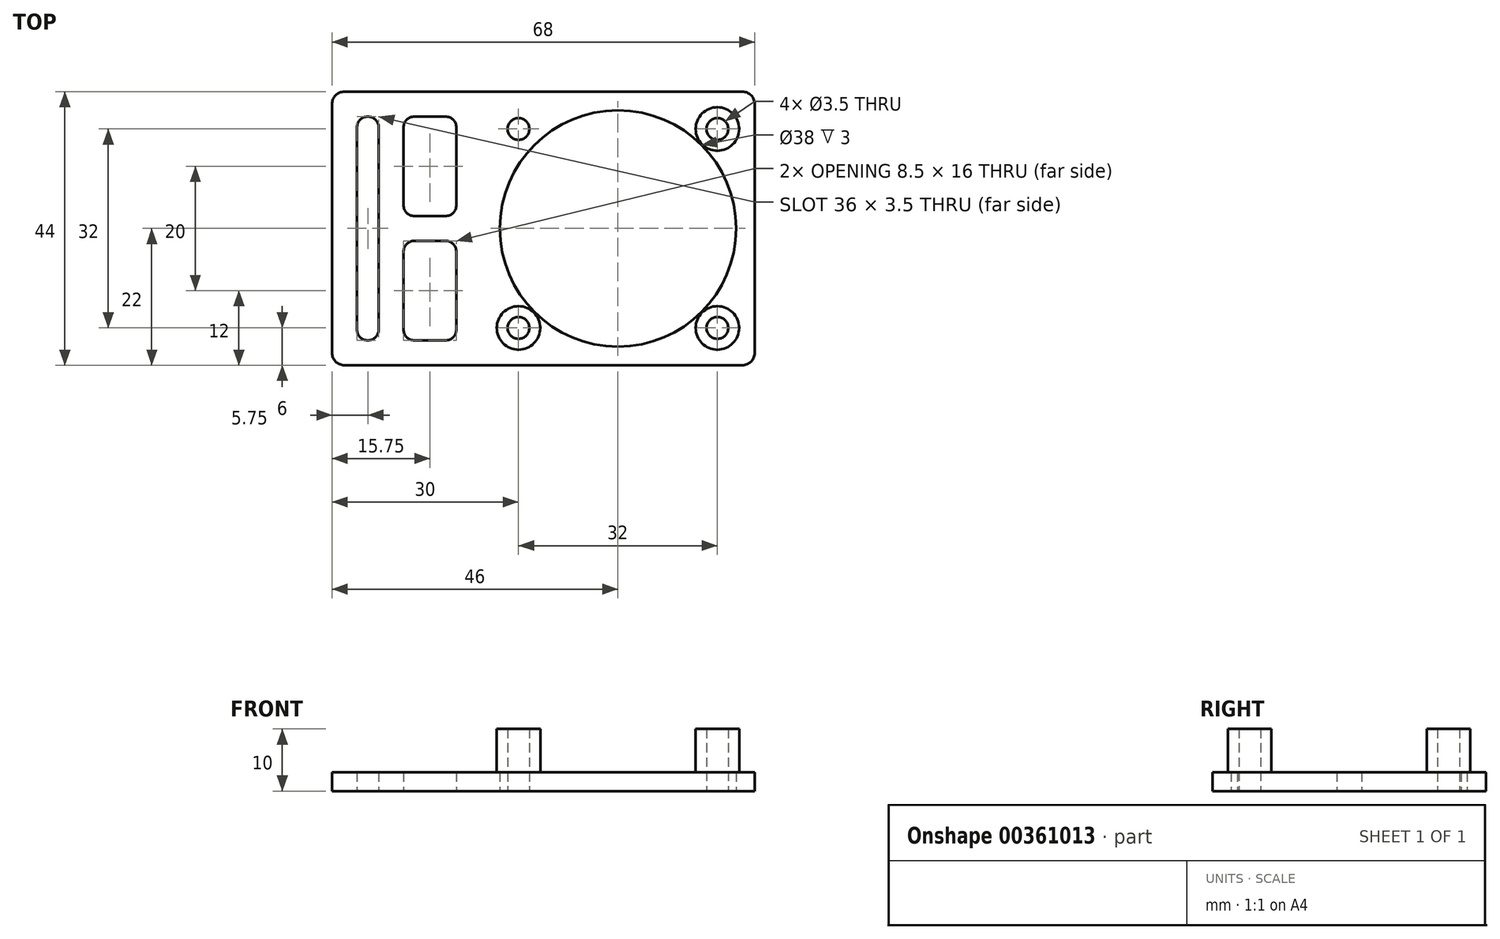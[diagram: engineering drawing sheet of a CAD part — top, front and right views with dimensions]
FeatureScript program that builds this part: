
annotation { "Feature Type Name" : "Feature", "Feature Type Description" : "" }
export const myFeature = defineFeature(function(context is Context, id is Id, definition is map)
    precondition{}
    {
        {
            var Q0;
            Q0=qCreatedBy(makeId("Top.planeOp"),FACE);
            var sketch = newSketch(context, id + "F0", { "sketchPlane" : qUnion([Q0])});
            skLineSegment(sketch, "E0.bottom", {"start": v(22, 22) * mm, "end": v(-22, 22) * mm});
            skLineSegment(sketch, "E0.top", {"start": v(22, -22) * mm, "end": v(-22, -22) * mm});
            skLineSegment(sketch, "E0.left", {"start": v(22, 22) * mm, "end": v(22, -22) * mm});
            skLineSegment(sketch, "E0.right", {"start": v(-22, 22) * mm, "end": v(-22, -22) * mm});
            skPoint(sketch, "E0.middle", {"position": v(0, 0) * mm});
            skCircle(sketch, "E1", {"center": v(0, 0) * mm, "radius": 19 * mm});
            skCircle(sketch, "E2", {"center": v(-16, 16) * mm, "radius": 1.75 * mm});
            skCircle(sketch, "E3", {"center": v(16, 16) * mm, "radius": 1.75 * mm});
            skCircle(sketch, "E4", {"center": v(-16, -16) * mm, "radius": 1.75 * mm});
            skCircle(sketch, "E5", {"center": v(16, -16) * mm, "radius": 1.75 * mm});
            skCircle(sketch, "E6", {"center": v(16, 16) * mm, "radius": 3.5 * mm});
            skCircle(sketch, "E7", {"center": v(16, -16) * mm, "radius": 3.5 * mm});
            skCircle(sketch, "E8", {"center": v(-16, -16) * mm, "radius": 3.5 * mm});
            skLineSegment(sketch, "E9", {"start": v(-22, 22) * mm, "end": v(-42, 22) * mm});
            skLineSegment(sketch, "E10", {"start": v(-42, 22) * mm, "end": v(-46, 22) * mm});
            skLineSegment(sketch, "E11", {"start": v(-46, 22) * mm, "end": v(-46, -22) * mm});
            skLineSegment(sketch, "E12", {"start": v(-46, -22) * mm, "end": v(-22, -22) * mm});
            skArc(sketch, "E13", {"start": v(-38.5, 16.25) * mm, "mid": v(-40.25, 18) * mm, "end": v(-42, 16.25) * mm});
            skArc(sketch, "E14", {"start": v(-42, -16.25) * mm, "mid": v(-40.25, -18) * mm, "end": v(-38.5, -16.25) * mm});
            skLineSegment(sketch, "E15", {"start": v(-38.5, -16.25) * mm, "end": v(-38.5, 16.25) * mm});
            skLineSegment(sketch, "E16", {"start": v(-42, -16.25) * mm, "end": v(-42, 16.25) * mm});
            skPoint(sketch, "E17.oppositeSnap0", {"position": v(-40.25, 18) * mm});
            skLineSegment(sketch, "E17.top", {"start": v(-34.5, 18) * mm, "end": v(-26, 18) * mm});
            skLineSegment(sketch, "E17.right", {"start": v(-26, -18) * mm, "end": v(-26, -2) * mm});
            skLineSegment(sketch, "E18", {"start": v(-34.5, -18) * mm, "end": v(-26, -18) * mm});
            skLineSegment(sketch, "E19", {"start": v(-34.5, -18) * mm, "end": v(-34.5, -2) * mm});
            skLineSegment(sketch, "E20", {"start": v(-34.5, -2) * mm, "end": v(-26, -2) * mm});
            skLineSegment(sketch, "E21", {"start": v(-34.5, 18) * mm, "end": v(-34.5, 2) * mm});
            skLineSegment(sketch, "E22", {"start": v(-34.5, 2) * mm, "end": v(-26, 2) * mm});
            skLineSegment(sketch, "E23.trimOffspring", {"start": v(-26, 2) * mm, "end": v(-26, 18) * mm});
            skSolve(sketch);
        }
        {
            var Q0;
            Q0=makeQuery(id+"F0.imprint","IMPRINT",FACE,{"disambiguationData":[TD([[makeQuery(id+"F0.imprint","IMPRINT",EDGE,{"derivedFrom":sQuery(id+"F0.wireOp",EDGE,"E0.bottom")}),1.0]])]});
            var Q1;
            Q1=makeQuery(id+"F0.imprint","IMPRINT",FACE,{"disambiguationData":[TD([[makeQuery(id+"F0.imprint","IMPRINT",EDGE,{"derivedFrom":sQuery(id+"F0.wireOp",EDGE,"E0.right")}),-1.0]])]});
            extrude(context, id + "F1", {"entities" : qUnion([Q0, Q1]), "depth" : 3 * mm});
        }
        {
            var Q0;
            Q0=makeQuery(id+"F0.imprint","IMPRINT",FACE,{"disambiguationData":[TD([[makeQuery(id+"F0.imprint","IMPRINT",EDGE,{"derivedFrom":sQuery(id+"F0.wireOp",EDGE,"E3")}),-1.0]])]});
            var Q1;
            Q1=makeQuery(id+"F0.imprint","IMPRINT",FACE,{"disambiguationData":[TD([[makeQuery(id+"F0.imprint","IMPRINT",EDGE,{"derivedFrom":sQuery(id+"F0.wireOp",EDGE,"E5")}),-1.0]])]});
            var Q2;
            Q2=makeQuery(id+"F0.imprint","IMPRINT",FACE,{"disambiguationData":[TD([[makeQuery(id+"F0.imprint","IMPRINT",EDGE,{"derivedFrom":sQuery(id+"F0.wireOp",EDGE,"E4")}),-1.0]])]});
            extrude(context, id + "F2", {"entities" : qUnion([Q0, Q1, Q2]), "operationType" : NewBodyOperationType.ADD, "depth" : 10 * mm});
        }
        {
            var Q0;
            Q0=makeQuery(id+"F1.opExtrude","SWEPT_EDGE",EDGE,{"disambiguationData":[OSD([sQuery(id+"F0.wireOp",EDGE,"E17.top"),sQuery(id+"F0.wireOp",EDGE,"E21")])]});
            var Q1;
            Q1=makeQuery(id+"F1.opExtrude","SWEPT_EDGE",EDGE,{"disambiguationData":[OSD([sQuery(id+"F0.wireOp",EDGE,"E17.top"),sQuery(id+"F0.wireOp",EDGE,"E23.trimOffspring")])]});
            var Q2;
            Q2=makeQuery(id+"F1.opExtrude","SWEPT_EDGE",EDGE,{"disambiguationData":[OSD([sQuery(id+"F0.wireOp",EDGE,"E21"),sQuery(id+"F0.wireOp",EDGE,"E22")])]});
            var Q3;
            Q3=makeQuery(id+"F1.opExtrude","SWEPT_EDGE",EDGE,{"disambiguationData":[OSD([sQuery(id+"F0.wireOp",EDGE,"E22"),sQuery(id+"F0.wireOp",EDGE,"E23.trimOffspring")])]});
            var Q4;
            Q4=makeQuery(id+"F1.opExtrude","SWEPT_EDGE",EDGE,{"disambiguationData":[OSD([sQuery(id+"F0.wireOp",EDGE,"E18"),sQuery(id+"F0.wireOp",EDGE,"E19")])]});
            var Q5;
            Q5=makeQuery(id+"F1.opExtrude","SWEPT_EDGE",EDGE,{"disambiguationData":[OSD([sQuery(id+"F0.wireOp",EDGE,"E17.right"),sQuery(id+"F0.wireOp",EDGE,"E18")])]});
            var Q6;
            Q6=makeQuery(id+"F1.opExtrude","SWEPT_EDGE",EDGE,{"disambiguationData":[OSD([sQuery(id+"F0.wireOp",EDGE,"E19"),sQuery(id+"F0.wireOp",EDGE,"E20")])]});
            var Q7;
            Q7=makeQuery(id+"F1.opExtrude","SWEPT_EDGE",EDGE,{"disambiguationData":[OSD([sQuery(id+"F0.wireOp",EDGE,"E17.right"),sQuery(id+"F0.wireOp",EDGE,"E20")])]});
            fillet(context, id + "F3", {"entities" : qUnion([Q0, Q1, Q2, Q3, Q4, Q5, Q6, Q7]), "radius" : 1.75 * mm, "tangentPropagation" : true, "allowEdgeOverflow" : false});
        }
        {
            var Q0;
            Q0=makeQuery(id+"F1.opExtrude","SWEPT_EDGE",EDGE,{"disambiguationData":[OSD([sQuery(id+"F0.wireOp",EDGE,"E10"),sQuery(id+"F0.wireOp",EDGE,"E11")])]});
            var Q1;
            Q1=makeQuery(id+"F1.opExtrude","SWEPT_EDGE",EDGE,{"disambiguationData":[OSD([sQuery(id+"F0.wireOp",EDGE,"E11"),sQuery(id+"F0.wireOp",EDGE,"E12")])]});
            var Q2;
            Q2=makeQuery(id+"F1.opExtrude","SWEPT_EDGE",EDGE,{"disambiguationData":[OSD([sQuery(id+"F0.wireOp",EDGE,"E0.top"),sQuery(id+"F0.wireOp",EDGE,"E0.left")])]});
            var Q3;
            Q3=makeQuery(id+"F1.opExtrude","SWEPT_EDGE",EDGE,{"disambiguationData":[OSD([sQuery(id+"F0.wireOp",EDGE,"E0.bottom"),sQuery(id+"F0.wireOp",EDGE,"E0.left")])]});
            fillet(context, id + "F4", {"entities" : qUnion([Q0, Q1, Q2, Q3]), "radius" : 2 * mm, "tangentPropagation" : true, "allowEdgeOverflow" : false});
        }
    });
